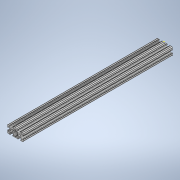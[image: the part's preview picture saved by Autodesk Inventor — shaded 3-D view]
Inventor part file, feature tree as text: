
AUTODESK INVENTOR PART (.ipt)
format: ipt  version: 2020 (Build 240168000, 168)  size: 333,824 bytes
history: native  units: in
note: dims shown in document units (in); Inventor stores cm internally (conversion verified against a paired STEP export)
features: sketch x2, extrude x1
ambient origin geometry x8: Origin, YZ Plane, XZ Plane, XY Plane, X Axis, Y Axis, Z Axis, Center Point
bodies: Solid1 (feature_tree)
feature tree (3):
  extrude  "Extrusion1"  [1 undecoded]
  sketch  "Sketch2"
  sketch  "Sketch1"  dims[d0=19.0in d1=0.0in]
note: 1 required parameter value undecoded (feature->parameter linkage not recoverable at this tier; creation-order binding heuristic only, values carry confidence <= 0.55)
